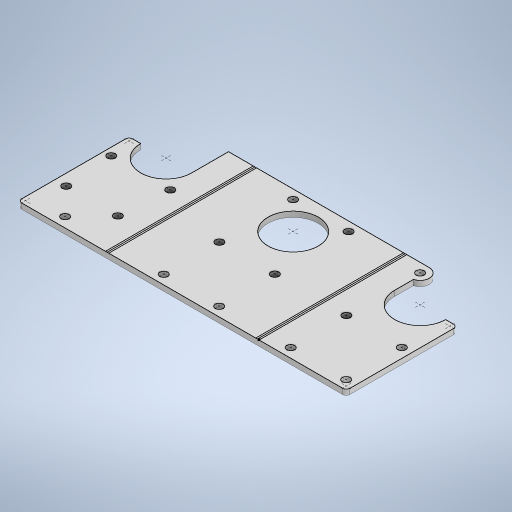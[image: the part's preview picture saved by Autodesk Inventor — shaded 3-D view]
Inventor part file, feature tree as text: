
AUTODESK INVENTOR PART (.ipt)
format: ipt  version: 2024.2 (Build 282272000, 272)  size: 297,472 bytes
history: native  units: in
note: dims shown in document units (in); Inventor stores cm internally (conversion verified against a paired STEP export)
features: sketch x1
ambient origin geometry x8: Origin, YZ Plane, XZ Plane, XY Plane, X Axis, Y Axis, Z Axis, Center Point
bodies: Solid1 (feature_tree)
feature tree (1):
  sketch  "Sketch1"  dims[d3=0.0591in d4=0.0in]
